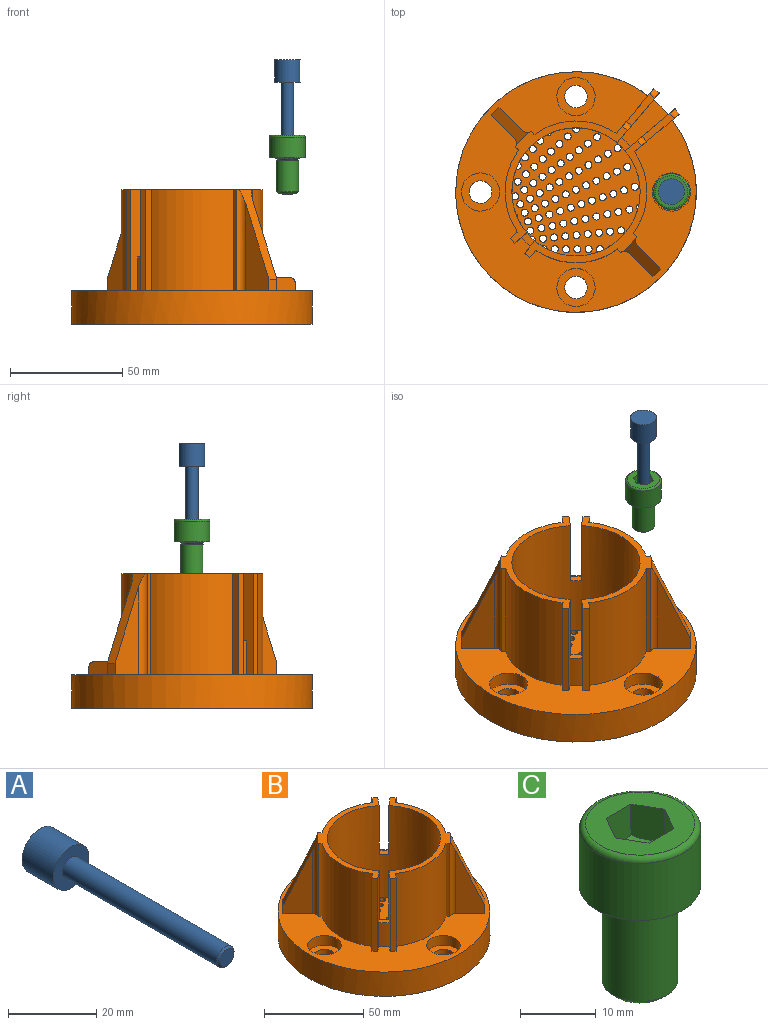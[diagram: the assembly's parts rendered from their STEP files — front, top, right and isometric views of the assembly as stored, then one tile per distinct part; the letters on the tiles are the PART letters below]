
ASSEMBLY  parts=3 mates=2
PART A: 6 faces, bbox 11.5x60x11.5 mm
  f0: cylinder r=2.75mm len=49.5mm, axis (0,1,0), area 855.3mm2, adj f3,f5
  f1: plane 4.5x4.5mm, normal (0,-1,0), area 15.9mm2, adj f5
  f2: cylinder r=5.75mm len=11.5mm, axis (0,1,0), area 361.3mm2, adj f3,f4
  f3: plane 11.5x11.5mm, normal (0,-1,0), area 80.1mm2, adj f0,f2
  f4: plane 11.5x11.5mm, normal (0,1,0), area 103.9mm2, adj f2
  f5: cone r=2.25mm half-angle=45deg, axis (0,1,0), area 11.1mm2, adj f0,f1
PART B: 180 faces, bbox 107.1x107.1x60 mm
  f0: cylinder r=53.56mm len=13.49mm, axis (0,0,-1), area 123.7mm2, adj f4,f38,f39,f177
  f1: plane 36.19x2.3mm, normal (0.77,0.64,0), area 108.6mm2, adj f15,f39,f165,f178
  f2: plane 107.11x107.11mm, normal (0,0,1), area 4435.2mm2, adj f5,f6,f7,f8,f26,f27,f28,f30
  f3: plane 36.19x2.3mm, normal (0.64,0.77,0), area 108.6mm2, adj f14,f38,f164,f173
  f4: plane 20.74x20.74mm, normal (0,0,1), area 163.4mm2, adj f0,f9,f38,f39
  f5: cylinder r=31.56mm len=15mm, axis (0,0,1), area 82.6mm2, adj f2,f25,f26,f27
  f6: cylinder r=31.56mm len=45mm, axis (0,0,1), area 1757mm2, adj f2,f14,f71,f166
  f7: cylinder r=31.56mm len=45mm, axis (0,0,1), area 1757mm2, adj f2,f15,f70,f169
  f8: cylinder r=31.56mm len=45mm, axis (0,0,1), area 1757mm2, adj f2,f15,f67,f165
  f9: cylinder r=31.56mm len=15mm, axis (0,0,1), area 82.6mm2, adj f4,f37,f38,f39
  f10: cylinder r=28.56mm len=60mm, axis (0,0,1), area 10039.2mm2, adj f14,f15,f24,f25,f26,f27,f37,f38
  f11: cylinder r=31.06mm len=51.18mm, axis (0,0,1), area 1157mm2, adj f24,f46,f72,f74
  f12: cylinder r=51.06mm len=85.35mm, axis (0,0,-1), area 1748.7mm2, adj f24,f46,f51,f52,f53,f54,f72,f74
  f13: plane 84.79x84.79mm, normal (0,0,-1), area 1770.4mm2, adj f40,f45,f48,f50,f73,f75
  f14: plane 54.41x54.41mm, normal (0,0,1), area 312.3mm2, adj f3,f6,f10,f27,f38,f61,f65,f66
  f15: plane 54.41x54.41mm, normal (0,0,1), area 312.3mm2, adj f1,f7,f8,f10,f26,f39,f55,f59
  f16: plane 15x15mm, normal (0,0,-1), area 98.2mm2, adj f23,f44
  f17: plane 15x15mm, normal (0,0,-1), area 98.2mm2, adj f22,f43
  f18: plane 15x15mm, normal (0,0,-1), area 98.2mm2, adj f21,f42
  f19: plane 15x15mm, normal (0,0,-1), area 98.2mm2, adj f20,f41
  f20: cylinder r=5mm len=10mm, axis (0,0,1), area 282.7mm2, adj f19,f35
  f21: cylinder r=5mm len=10mm, axis (0,0,1), area 282.7mm2, adj f18,f33
  f22: cylinder r=5mm len=10mm, axis (0,0,1), area 282.7mm2, adj f17,f31
  f23: cylinder r=5mm len=10mm, axis (0,0,1), area 282.7mm2, adj f16,f29
  f24: plane 107.11x107.11mm, normal (0,0,-1), area 3362mm2, adj f10,f11,f12,f28,f40,f45,f72,f73
  f25: plane 5.82x5.82mm, normal (0,0,1), area 15.7mm2, adj f5,f10,f26,f27
  f26: plane 45x5.36mm, normal (-0.77,0.64,0), area 270mm2, adj f2,f5,f10,f15,f25,f168
  f27: plane 45x5.36mm, normal (0.64,-0.77,0), area 270mm2, adj f2,f5,f10,f14,f25,f167
  f28: cylinder r=53.56mm len=107.11mm, axis (0,0,-1), area 4791mm2, adj f2,f24,f164,f165,f177
  f29: plane 17x17mm, normal (0,0,1), area 148.4mm2, adj f23,f30
  f30: cylinder r=8.5mm len=17mm, axis (0,0,1), area 320.4mm2, adj f2,f29
  f31: plane 17x17mm, normal (0,0,1), area 148.4mm2, adj f22,f32
  f32: cylinder r=8.5mm len=17mm, axis (0,0,1), area 320.4mm2, adj f2,f31
  f33: plane 17x17mm, normal (0,0,1), area 148.4mm2, adj f21,f34
  f34: cylinder r=8.5mm len=17mm, axis (0,0,1), area 320.4mm2, adj f2,f33
  f35: plane 17x17mm, normal (0,0,1), area 148.4mm2, adj f20,f36
  f36: cylinder r=8.5mm len=17mm, axis (0,0,1), area 320.4mm2, adj f2,f35
  f37: plane 5.82x5.82mm, normal (0,0,1), area 15.7mm2, adj f9,f10,f38,f39
  f38: plane 58.49x22.22mm, normal (0.77,-0.64,0), area 441.4mm2, adj f0,f3,f4,f9,f10,f14,f37,f170
  f39: plane 58.1x22.22mm, normal (-0.64,0.77,0), area 446.3mm2, adj f0,f1,f4,f9,f10,f15,f37,f175
  f40: cylinder r=31.06mm len=51.18mm, axis (0,0,1), area 1157mm2, adj f13,f24,f73,f75
  f41: cylinder r=7.5mm len=15mm, axis (0,0,1), area 306.3mm2, adj f19,f53
  f42: cylinder r=7.5mm len=15mm, axis (0,0,1), area 306.3mm2, adj f18,f51
  f43: cylinder r=7.5mm len=15mm, axis (0,0,1), area 306.3mm2, adj f17,f49
  f44: cylinder r=7.5mm len=15mm, axis (0,0,1), area 306.3mm2, adj f16,f47
  f45: cylinder r=51.06mm len=85.35mm, axis (0,0,-1), area 1760.4mm2, adj f13,f24,f47,f48,f49,f50,f73,f75
  f46: plane 84.79x84.79mm, normal (0,0,-1), area 1770.4mm2, adj f11,f12,f52,f54,f72,f74
  f47: plane 22x19.56mm, normal (0,0,-1), area 177.9mm2, adj f44,f45,f48
  f48: cylinder r=11mm len=22mm, axis (0,0,1), area 314.7mm2, adj f13,f45,f47
  f49: plane 22x19.56mm, normal (0,0,-1), area 177.9mm2, adj f43,f45,f50
  f50: cylinder r=11mm len=22mm, axis (0,0,1), area 314.7mm2, adj f13,f45,f49
  f51: plane 22x19.56mm, normal (0,0,-1), area 177.9mm2, adj f12,f42,f52
  f52: cylinder r=11mm len=22mm, axis (0,0,1), area 314.7mm2, adj f12,f46,f51
  f53: plane 22x19.56mm, normal (0,0,-1), area 177.9mm2, adj f12,f41,f54
  f54: cylinder r=11mm len=22mm, axis (0,0,1), area 314.7mm2, adj f12,f46,f53
  f55: plane 39.85x16.9mm, normal (0.65,-0.65,0.4), area 223mm2, adj f15,f56,f57,f58,f59,f60
  f56: plane 5.15x3.54mm, normal (0.71,-0.71,0), area 25.8mm2, adj f2,f55,f57,f58
  f57: plane 39.09x10.5mm, normal (0.71,0.71,0), area 328.4mm2, adj f2,f55,f56,f59
  f58: plane 39.09x10.5mm, normal (-0.71,-0.71,0), area 328.4mm2, adj f2,f55,f56,f60
  f59: cylinder r=3mm len=45mm, axis (0,0,1), area 183.4mm2, adj f2,f15,f55,f57,f67
  f60: cylinder r=3mm len=45mm, axis (0,0,1), area 183.4mm2, adj f2,f15,f55,f58,f70
  f61: plane 39.85x16.9mm, normal (-0.65,0.65,0.4), area 223mm2, adj f14,f62,f63,f64,f65,f66
  f62: plane 5.15x3.54mm, normal (-0.71,0.71,0), area 25.8mm2, adj f2,f61,f63,f64
  f63: plane 39.09x10.5mm, normal (-0.71,-0.71,0), area 328.4mm2, adj f2,f61,f62,f65
  f64: plane 39.09x10.5mm, normal (0.71,0.71,0), area 328.4mm2, adj f2,f61,f62,f66
  f65: cylinder r=3mm len=45mm, axis (0,0,1), area 183.4mm2, adj f2,f14,f61,f63,f71
  f66: cylinder r=3mm len=45mm, axis (0,0,1), area 183.4mm2, adj f2,f14,f61,f64,f68
  f67: plane 45x1.61mm, normal (0.59,0.81,0), area 90mm2, adj f2,f8,f15,f59
  f68: plane 45x1.61mm, normal (0.81,0.59,0), area 90mm2, adj f2,f14,f66,f69
  f69: cylinder r=31.56mm len=45mm, axis (0,0,1), area 1757mm2, adj f2,f14,f68,f164
  f70: plane 45x1.61mm, normal (-0.81,-0.59,0), area 90mm2, adj f2,f7,f15,f60
  f71: plane 45x1.61mm, normal (-0.59,-0.81,0), area 90mm2, adj f2,f6,f14,f65
  f72: plane 14.17x14.17mm, normal (0.71,0.71,0), area 250.5mm2, adj f11,f12,f24,f46
  f73: plane 14.17x14.17mm, normal (-0.71,-0.71,0), area 250.5mm2, adj f13,f24,f40,f45
  f74: plane 14.17x14.17mm, normal (0.71,0.71,0), area 250.5mm2, adj f11,f12,f24,f46
  f75: plane 14.17x14.17mm, normal (-0.71,-0.71,0), area 250.5mm2, adj f13,f24,f40,f45
  f76: cylinder r=1.57mm len=3mm, axis (0,0,-1), area 10.4mm2, adj f10,f24,f93
  f77: cylinder r=1.57mm len=3mm, axis (0,0,-1), area 9.2mm2, adj f10,f24,f93
  f78: cylinder r=1.57mm len=3mm, axis (0,0,-1), area 12.3mm2, adj f10,f24,f93
  f79: cylinder r=1.57mm len=3mm, axis (0,0,-1), area 1.9mm2, adj f10,f24,f93
  f80: cylinder r=1.57mm len=3.15mm, axis (0,0,-1), area 17.4mm2, adj f10,f24,f93
  f81: cylinder r=1.57mm len=3.15mm, axis (0,0,-1), area 25.7mm2, adj f10,f24,f93
  f82: cylinder r=1.57mm len=3.15mm, axis (0,0,-1), area 21.1mm2, adj f10,f24,f93
  f83: cylinder r=1.57mm len=3.12mm, axis (0,0,-1), area 19mm2, adj f10,f24,f93
  f84: cylinder r=1.57mm len=3mm, axis (0,0,-1), area 9.3mm2, adj f10,f24,f93
  f85: cylinder r=1.57mm len=3.02mm, axis (0,0,-1), area 15.1mm2, adj f10,f24,f93
  f86: cylinder r=1.57mm len=3.15mm, axis (0,0,-1), area 25.5mm2, adj f10,f24,f93
  f87: cylinder r=1.57mm len=3.15mm, axis (0,0,-1), area 22.8mm2, adj f10,f24,f93
  f88: cylinder r=1.57mm len=3.15mm, axis (0,0,-1), area 25.1mm2, adj f10,f24,f93
  f89: cylinder r=1.57mm len=3mm, axis (0,0,-1), area 5.6mm2, adj f10,f24,f93
  f90: cylinder r=1.57mm len=3mm, axis (0,0,-1), area 7.5mm2, adj f10,f24,f93
  f91: cylinder r=1.57mm len=3mm, axis (0,0,-1), area 6.9mm2, adj f10,f24,f93
  f92: cylinder r=1.57mm len=3mm, axis (0,0,-1), area 4.6mm2, adj f10,f24,f93
  f93: plane 57.11x57.08mm, normal (0,0,1), area 1956.5mm2, adj f10,f76,f77,f78,f79,f80,f81,f82
  f94: cylinder r=1.57mm len=3.15mm, axis (0,0,-1), area 29.6mm2, adj f24,f93
  f95: cylinder r=1.57mm len=3.15mm, axis (0,0,-1), area 29.6mm2, adj f24,f93
  f96: cylinder r=1.57mm len=3.15mm, axis (0,0,-1), area 29.6mm2, adj f24,f93
  f97: cylinder r=1.57mm len=3.15mm, axis (0,0,-1), area 29.6mm2, adj f24,f93
  f98: cylinder r=1.57mm len=3.15mm, axis (0,0,-1), area 29.6mm2, adj f24,f93
  f99: cylinder r=1.57mm len=3.15mm, axis (0,0,-1), area 29.6mm2, adj f24,f93
  f100: cylinder r=1.57mm len=3.15mm, axis (0,0,-1), area 29.6mm2, adj f24,f93
  f101: cylinder r=1.57mm len=3.15mm, axis (0,0,-1), area 29.6mm2, adj f24,f93
  f102: cylinder r=1.57mm len=3.15mm, axis (0,0,-1), area 29.6mm2, adj f24,f93
  f103: cylinder r=1.57mm len=3.15mm, axis (0,0,-1), area 29.6mm2, adj f24,f93
  f104: cylinder r=1.57mm len=3.15mm, axis (0,0,-1), area 29.6mm2, adj f24,f93
  f105: cylinder r=1.57mm len=3.15mm, axis (0,0,-1), area 29.6mm2, adj f24,f93
  f106: cylinder r=1.57mm len=3.15mm, axis (0,0,-1), area 29.6mm2, adj f24,f93
  f107: cylinder r=1.57mm len=3.15mm, axis (0,0,-1), area 29.6mm2, adj f24,f93
  f108: cylinder r=1.57mm len=3.15mm, axis (0,0,-1), area 29.6mm2, adj f24,f93
  f109: cylinder r=1.57mm len=3.15mm, axis (0,0,-1), area 29.6mm2, adj f24,f93
  f110: cylinder r=1.57mm len=3.15mm, axis (0,0,-1), area 29.6mm2, adj f24,f93
  f111: cylinder r=1.57mm len=3.15mm, axis (0,0,-1), area 29.6mm2, adj f24,f93
  f112: cylinder r=1.57mm len=3.15mm, axis (0,0,-1), area 29.6mm2, adj f24,f93
  f113: cylinder r=1.57mm len=3.15mm, axis (0,0,-1), area 29.6mm2, adj f24,f93
  f114: cylinder r=1.57mm len=3.15mm, axis (0,0,-1), area 29.6mm2, adj f24,f93
  f115: cylinder r=1.57mm len=3.15mm, axis (0,0,-1), area 29.6mm2, adj f24,f93
  f116: cylinder r=1.57mm len=3.15mm, axis (0,0,-1), area 29.6mm2, adj f24,f93
  f117: cylinder r=1.57mm len=3.15mm, axis (0,0,-1), area 29.6mm2, adj f24,f93
  f118: cylinder r=1.57mm len=3.15mm, axis (0,0,-1), area 29.6mm2, adj f24,f93
  f119: cylinder r=1.57mm len=3.15mm, axis (0,0,-1), area 29.6mm2, adj f24,f93
  f120: cylinder r=1.57mm len=3.15mm, axis (0,0,-1), area 29.6mm2, adj f24,f93
  f121: cylinder r=1.57mm len=3.15mm, axis (0,0,-1), area 29.6mm2, adj f24,f93
  f122: cylinder r=1.57mm len=3.15mm, axis (0,0,-1), area 29.6mm2, adj f24,f93
  f123: cylinder r=1.57mm len=3.15mm, axis (0,0,-1), area 29.6mm2, adj f24,f93
  f124: cylinder r=1.57mm len=3.15mm, axis (0,0,-1), area 29.6mm2, adj f24,f93
  f125: cylinder r=1.57mm len=3.15mm, axis (0,0,-1), area 29.6mm2, adj f24,f93
  f126: cylinder r=1.57mm len=3.15mm, axis (0,0,-1), area 29.6mm2, adj f24,f93
  f127: cylinder r=1.57mm len=3.15mm, axis (0,0,-1), area 29.6mm2, adj f24,f93
  f128: cylinder r=1.57mm len=3.15mm, axis (0,0,-1), area 29.6mm2, adj f24,f93
  f129: cylinder r=1.57mm len=3.15mm, axis (0,0,-1), area 29.6mm2, adj f24,f93
  f130: cylinder r=1.57mm len=3.15mm, axis (0,0,-1), area 29.6mm2, adj f24,f93
  f131: cylinder r=1.57mm len=3.15mm, axis (0,0,-1), area 29.6mm2, adj f24,f93
  f132: cylinder r=1.57mm len=3.15mm, axis (0,0,-1), area 29.6mm2, adj f24,f93
  f133: cylinder r=1.57mm len=3.15mm, axis (0,0,-1), area 29.6mm2, adj f24,f93
  f134: cylinder r=1.57mm len=3.15mm, axis (0,0,-1), area 29.6mm2, adj f24,f93
  f135: cylinder r=1.57mm len=3.15mm, axis (0,0,-1), area 29.6mm2, adj f24,f93
  f136: cylinder r=1.57mm len=3.15mm, axis (0,0,-1), area 29.6mm2, adj f24,f93
  f137: cylinder r=1.57mm len=3.15mm, axis (0,0,-1), area 29.6mm2, adj f24,f93
  f138: cylinder r=1.57mm len=3.15mm, axis (0,0,-1), area 29.6mm2, adj f24,f93
  f139: cylinder r=1.57mm len=3.15mm, axis (0,0,-1), area 29.6mm2, adj f24,f93
  f140: cylinder r=1.57mm len=3.15mm, axis (0,0,-1), area 29.6mm2, adj f24,f93
  f141: cylinder r=1.57mm len=3.15mm, axis (0,0,-1), area 29.6mm2, adj f24,f93
  f142: cylinder r=1.57mm len=3.15mm, axis (0,0,-1), area 29.6mm2, adj f24,f93
  f143: cylinder r=1.57mm len=3.15mm, axis (0,0,-1), area 29.6mm2, adj f24,f93
  f144: cylinder r=1.57mm len=3.15mm, axis (0,0,-1), area 29.6mm2, adj f24,f93
  f145: cylinder r=1.57mm len=3.15mm, axis (0,0,-1), area 29.6mm2, adj f24,f93
  f146: cylinder r=1.57mm len=3.15mm, axis (0,0,-1), area 29.6mm2, adj f24,f93
  f147: cylinder r=1.57mm len=3.15mm, axis (0,0,-1), area 29.6mm2, adj f24,f93
  f148: cylinder r=1.57mm len=3.15mm, axis (0,0,-1), area 29.6mm2, adj f24,f93
  f149: cylinder r=1.57mm len=3.15mm, axis (0,0,-1), area 29.6mm2, adj f24,f93
  f150: cylinder r=1.57mm len=3.15mm, axis (0,0,-1), area 29.6mm2, adj f24,f93
  f151: cylinder r=1.57mm len=3.15mm, axis (0,0,-1), area 29.6mm2, adj f24,f93
  f152: cylinder r=1.57mm len=3.15mm, axis (0,0,-1), area 29.6mm2, adj f24,f93
  f153: cylinder r=1.57mm len=3.15mm, axis (0,0,-1), area 29.6mm2, adj f24,f93
  f154: cylinder r=1.57mm len=3.15mm, axis (0,0,-1), area 29.6mm2, adj f24,f93
  f155: cylinder r=1.57mm len=3.15mm, axis (0,0,-1), area 29.6mm2, adj f24,f93
  f156: cylinder r=1.57mm len=3.15mm, axis (0,0,-1), area 29.6mm2, adj f24,f93
  f157: cylinder r=1.57mm len=3.15mm, axis (0,0,-1), area 29.6mm2, adj f24,f93
  f158: cylinder r=1.57mm len=3.15mm, axis (0,0,-1), area 29.6mm2, adj f24,f93
  f159: cylinder r=1.57mm len=3.15mm, axis (0,0,-1), area 29.6mm2, adj f24,f93
  f160: cylinder r=1.57mm len=3.15mm, axis (0,0,-1), area 29.6mm2, adj f24,f93
  f161: cylinder r=1.57mm len=3.15mm, axis (0,0,-1), area 29.6mm2, adj f24,f93
  f162: cylinder r=1.57mm len=3.15mm, axis (0,0,-1), area 29.6mm2, adj f24,f93
  f163: cylinder r=1.57mm len=3.15mm, axis (0,0,-1), area 29.6mm2, adj f24,f93
  f164: plane 58.77x20.03mm, normal (-0.77,0.64,0), area 359.3mm2, adj f2,f3,f14,f28,f69,f170,f171,f172
  f165: plane 58.14x20.03mm, normal (0.64,-0.77,0), area 363.9mm2, adj f1,f2,f8,f15,f28,f175,f176,f177
  f166: plane 45x3.17mm, normal (-0.64,0.77,0), area 186.4mm2, adj f2,f6,f14,f167
  f167: plane 45x2.3mm, normal (-0.77,-0.64,0), area 135mm2, adj f2,f14,f27,f166
  f168: plane 45x2.3mm, normal (-0.64,-0.77,0), area 135mm2, adj f2,f15,f26,f169
  f169: plane 45x3.17mm, normal (0.77,-0.64,0), area 186.4mm2, adj f2,f7,f15,f168
  f170: plane 14.19x12.58mm, normal (0,0,1), area 48mm2, adj f38,f164,f173,f174
  f171: plane 9.81x2.3mm, normal (0.64,0.77,0), area 29.4mm2, adj f38,f164,f172,f174
  f172: plane 6.25x4.21mm, normal (0.58,0.69,-0.43), area 20.2mm2, adj f38,f164,f171,f177
  f173: cylinder r=3mm len=4.23mm, axis (-0.77,0.64,0), area 14.1mm2, adj f3,f38,f164,f170
  f174: cylinder r=3mm len=4.23mm, axis (0.77,-0.64,0), area 14.1mm2, adj f38,f164,f170,f171
  f175: plane 14.19x12.58mm, normal (0,0,1), area 48mm2, adj f39,f165,f178,f179
  f176: plane 14.01x2.3mm, normal (0.77,0.64,0), area 42mm2, adj f39,f165,f177,f179
  f177: plane 31.12x26.11mm, normal (0.33,0.28,-0.9), area 110.7mm2, adj f0,f12,f24,f28,f38,f39,f164,f165
  f178: cylinder r=3mm len=4.23mm, axis (-0.64,0.77,0), area 14.1mm2, adj f1,f39,f165,f175
  f179: cylinder r=3mm len=4.23mm, axis (-0.64,0.77,0), area 14.1mm2, adj f39,f165,f175,f176
PART C: 18 faces, bbox 17.3x17.3x26 mm
  f0: cone r=4.59mm half-angle=45deg, axis (0,0,1), area 33.1mm2, adj f1,f16
  f1: cylinder r=5mm len=13.83mm, axis (0,0,-1), area 434.4mm2, adj f0,f15
  f2: cone r=4.59mm half-angle=45deg, axis (0,0,1), area 33.1mm2, adj f3,f15
  f3: cylinder r=5mm len=10mm, axis (0,0,-1), area 1.6mm2, adj f2,f4
  f4: torus R=5.5mm, axis (0,0,-1), area 25.6mm2, adj f3,f14
  f5: cylinder r=8mm len=16mm, axis (0,0,-1), area 462.4mm2, adj f6,f14
  f6: torus R=7.2mm, axis (0,0,-1), area 60.9mm2, adj f5,f17
  f7: cone r=2.31mm half-angle=60deg, axis (0,0,1), area 64mm2, adj f8,f9,f10,f11,f12,f13
  f8: plane 5.53x4mm, normal (0.87,0.5,0), area 24.2mm2, adj f7,f9,f13,f17
  f9: plane 5.53x4.62mm, normal (0,1,0), area 24.2mm2, adj f7,f8,f10,f17
  f10: plane 5.53x4mm, normal (-0.87,0.5,0), area 24.2mm2, adj f7,f9,f11,f17
  f11: plane 5.53x4mm, normal (-0.87,-0.5,0), area 24.2mm2, adj f7,f10,f12,f17
  f12: plane 5.41x4.62mm, normal (0,-1,0), area 24.2mm2, adj f7,f11,f13,f17
  f13: plane 5.53x4mm, normal (0.87,-0.5,0), area 24.2mm2, adj f7,f8,f12,f17
  f14: plane 16x16mm, normal (0,0,-1), area 106mm2, adj f4,f5
  f15: plane 10x10mm, normal (0,0,1), area 23.4mm2, adj f1,f2
  f16: plane 8.38x8.38mm, normal (0,0,-1), area 55.1mm2, adj f0
  f17: plane 14.4x14.4mm, normal (0,0,1), area 107.4mm2, adj f6,f8,f9,f10,f11,f12,f13
PLACE A rot(axis=(1,0,0),90deg) t=(31.35,30.77,45.18)mm
PLACE B t=(-11.15,-18.23,12.32)mm fixed
PLACE C rot(axis=(0.02,0,1),0deg) t=(31.35,-18.23,26.5)mm
MATE cylindrical C.f4 <-> B.f21  axis (0,0,-1) through (31.35,-18.23,-38.68)mm
MATE cylindrical A.f0 <-> C.f1  axis (0,0,1) through (31.35,-18.23,10.68)mm
